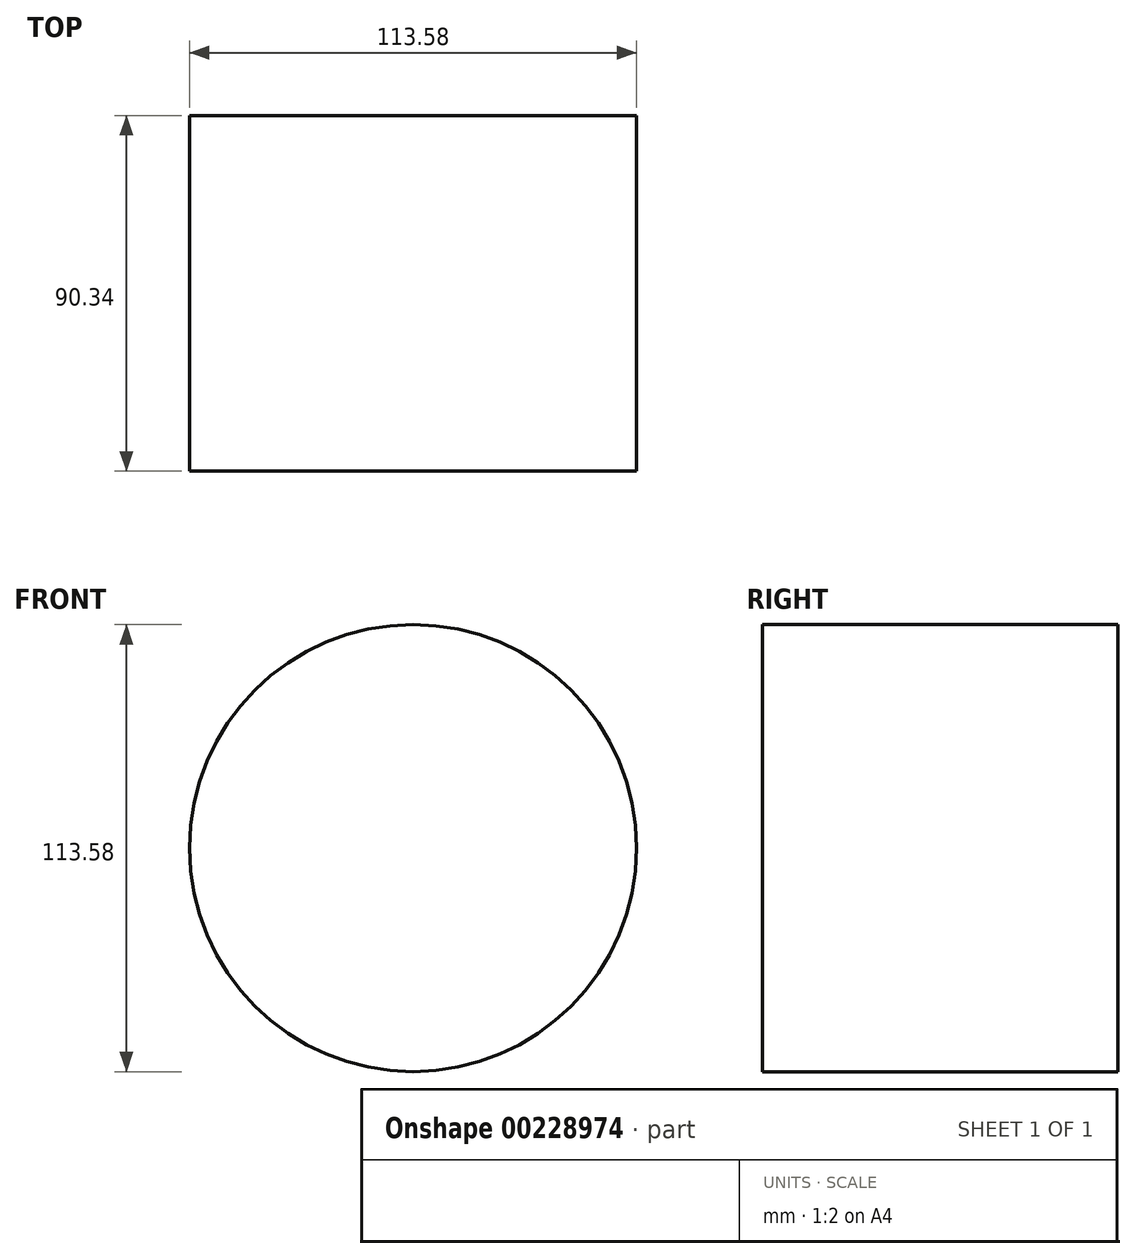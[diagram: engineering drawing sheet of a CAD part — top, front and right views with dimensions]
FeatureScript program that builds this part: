
annotation { "Feature Type Name" : "Feature", "Feature Type Description" : "" }
export const myFeature = defineFeature(function(context is Context, id is Id, definition is map)
    precondition{}
    {
        {
            var Q0;
            Q0=qCreatedBy(makeId("Front.planeOp"),FACE);
            var sketch = newSketch(context, id + "F0", { "sketchPlane" : qUnion([Q0])});
            skCircle(sketch, "E0", {"center": v(0, 0) * mm, "radius": 56.79 * mm});
            skSolve(sketch);
        }
        {
            var Q0;
            Q0=makeQuery(id+"F0.imprint","IMPRINT",FACE,{"disambiguationData":[TD([[makeQuery(id+"F0.imprint","IMPRINT",EDGE,{"derivedFrom":sQuery(id+"F0.wireOp",EDGE,"E0")}),1.0]])]});
            extrude(context, id + "F1", {"entities" : qUnion([Q0]), "depth" : 90.34 * mm});
        }
    });
